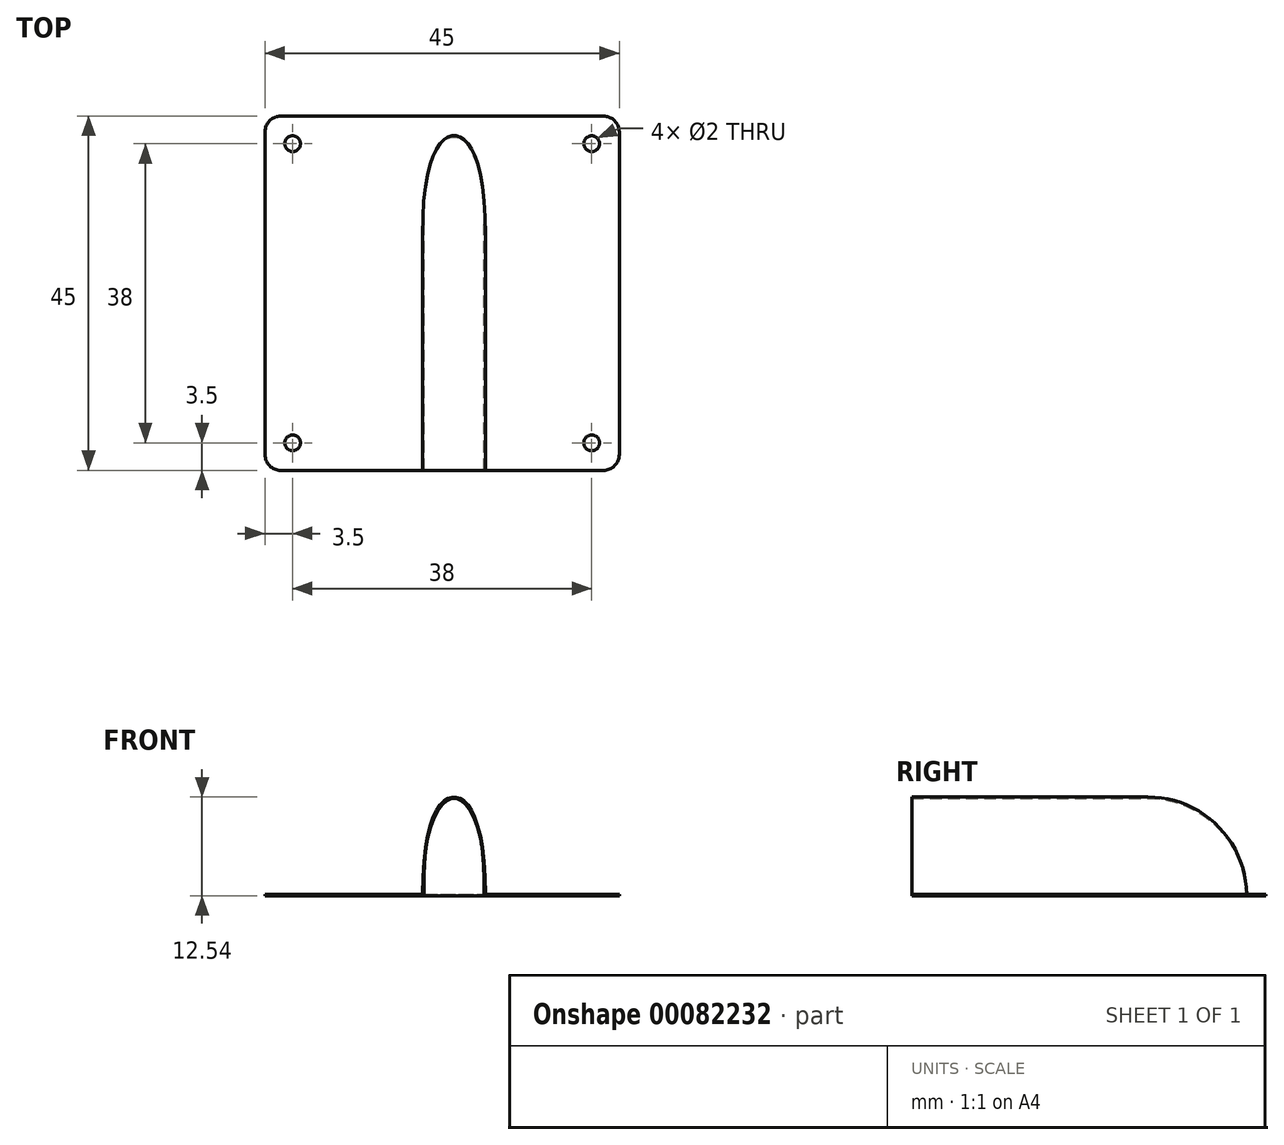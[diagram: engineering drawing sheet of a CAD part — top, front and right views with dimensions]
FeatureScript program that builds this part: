
annotation { "Feature Type Name" : "Feature", "Feature Type Description" : "" }
export const myFeature = defineFeature(function(context is Context, id is Id, definition is map)
    precondition{}
    {
        {
            var Q0;
            Q0=qCreatedBy(makeId("Top.planeOp"),FACE);
            var sketch = newSketch(context, id + "F0", { "sketchPlane" : qUnion([Q0])});
            skLineSegment(sketch, "E0.bottom", {"start": v(2, 45) * mm, "end": v(43, 45) * mm});
            skLineSegment(sketch, "E0.top", {"start": v(2, 0) * mm, "end": v(20, 0) * mm});
            skLineSegment(sketch, "E0.left", {"start": v(0, 43) * mm, "end": v(0, 2) * mm});
            skLineSegment(sketch, "E0.right", {"start": v(45, 43) * mm, "end": v(45, 2) * mm});
            skLineSegment(sketch, "E1.trimOffspring", {"start": v(28, 0) * mm, "end": v(43, 0) * mm});
            skCircle(sketch, "E2", {"center": v(3.5, 41.5) * mm, "radius": 1 * mm});
            skCircle(sketch, "E3", {"center": v(41.5, 41.5) * mm, "radius": 1 * mm});
            skCircle(sketch, "E4", {"center": v(41.5, 3.5) * mm, "radius": 1 * mm});
            skCircle(sketch, "E5", {"center": v(3.5, 3.5) * mm, "radius": 1 * mm});
            skLineSegment(sketch, "E6", {"start": v(20, 0) * mm, "end": v(20, 30) * mm});
            skLineSegment(sketch, "E7", {"start": v(28, 30) * mm, "end": v(28, 0) * mm});
            skPoint(sketch, "E8.visualSharp", {"position": v(0, 45) * mm});
            skArc(sketch, "E8.filletArc", {"start": v(2, 45) * mm, "mid": v(0.59, 44.41) * mm, "end": v(0, 43) * mm});
            skPoint(sketch, "E9.visualSharp", {"position": v(45, 45) * mm});
            skArc(sketch, "E9.filletArc", {"start": v(45, 43) * mm, "mid": v(44.41, 44.41) * mm, "end": v(43, 45) * mm});
            skPoint(sketch, "E10.visualSharp", {"position": v(45, 0) * mm});
            skArc(sketch, "E10.filletArc", {"start": v(43, 0) * mm, "mid": v(44.41, 0.59) * mm, "end": v(45, 2) * mm});
            skPoint(sketch, "E11.visualSharp", {"position": v(0, 0) * mm});
            skArc(sketch, "E11.filletArc", {"start": v(0, 2) * mm, "mid": v(0.59, 0.59) * mm, "end": v(2, 0) * mm});
            skFitSpline(sketch, "E12", {"points": [v(20, 30) * mm, v(24, 42.54) * mm, v(28, 30) * mm], "startDerivative": vector(0, 54.87) * mm, "endDerivative": vector(0, -54.87) * mm});
            skSolve(sketch);
        }
        {
            var Q0;
            Q0=makeQuery(id+"F0.imprint","IMPRINT",FACE,{"disambiguationData":[TD([[makeQuery(id+"F0.imprint","IMPRINT",EDGE,{"derivedFrom":sQuery(id+"F0.wireOp",EDGE,"E0.bottom")}),-1.0]])]});
            extrude(context, id + "F1", {"entities" : qUnion([Q0]), "depth" : .2 * mm});
        }
        {
            var Q0;
            Q0=qCreatedBy(makeId("Top.planeOp"),FACE);
            var sketch = newSketch(context, id + "F2", { "sketchPlane" : qUnion([Q0])});
            skFitSpline(sketch, "E13", {"points": [v(20, 30) * mm, v(24, 42.54) * mm, v(28, 30) * mm], "startDerivative": vector(0, 54.87) * mm, "endDerivative": vector(0, -54.87) * mm});
            skFitSpline(sketch, "E14.0", {"points": [v(20.2, 30) * mm, v(20.2, 32.28) * mm, v(20.45, 36.12) * mm, v(21.22, 39.29) * mm, v(22.02, 40.95) * mm, v(22.67, 41.79) * mm, v(23.34, 42.25) * mm, v(24, 42.39) * mm, v(24.66, 42.25) * mm, v(25.33, 41.79) * mm, v(25.98, 40.95) * mm, v(26.78, 39.29) * mm, v(27.55, 36.12) * mm, v(27.8, 32.28) * mm, v(27.8, 30) * mm]});
            skLineSegment(sketch, "E15", {"start": v(20, 30) * mm, "end": v(20.2, 30) * mm});
            skLineSegment(sketch, "E16", {"start": v(27.8, 30) * mm, "end": v(28, 30) * mm});
            skSolve(sketch);
        }
        {
            var Q0;
            Q0=qCreatedBy(makeId("Top.planeOp"),FACE);
            var sketch = newSketch(context, id + "F3", { "sketchPlane" : qUnion([Q0])});
            skLineSegment(sketch, "E17", {"start": v(20, 30) * mm, "end": v(28, 30) * mm});
            skSolve(sketch);
        }
        {
            var Q0;
            Q0=makeQuery(id+"F2.imprint","IMPRINT",FACE,{"disambiguationData":[TD([[makeQuery(id+"F2.imprint","IMPRINT",EDGE,{"derivedFrom":sQuery(id+"F2.wireOp",EDGE,"E13")}),-1.0]])]});
            var Q1;
            Q1=sQuery(id+"F3.wireOp",EDGE,"E17");
            revolve(context, id + "F4", {"operationType" : NewBodyOperationType.ADD, "entities" : qUnion([Q0]), "axis" : qUnion([Q1]), "revolveType" : RevolveType.ONE_DIRECTION, "angle" : 90 * degree});
        }
        {
            var Q0;
            Q0=makeQuery(id+"F4.opRevolve","CAP_FACE",FACE,{"disambiguationData":[OSD([sQuery(id+"F2.wireOp",EDGE,"E13"),sQuery(id+"F2.wireOp",EDGE,"E14.0"),sQuery(id+"F2.wireOp",EDGE,"E15"),sQuery(id+"F2.wireOp",EDGE,"E16")])],"isStart":false});
            extrude(context, id + "F5", {"entities" : qUnion([Q0]), "operationType" : NewBodyOperationType.ADD, "depth" : 30 * mm});
        }
    });
